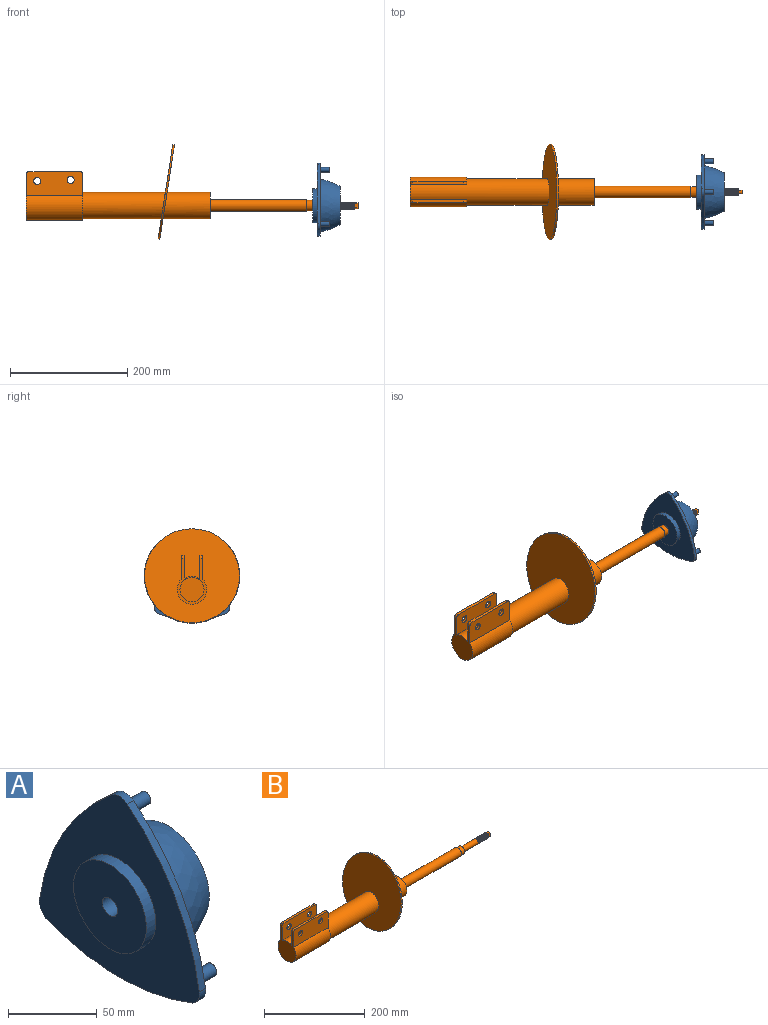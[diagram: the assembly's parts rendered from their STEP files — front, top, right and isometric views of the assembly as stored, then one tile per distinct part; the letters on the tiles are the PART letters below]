
ASSEMBLY  parts=2 mates=1
PART A: 19 faces, bbox 46.5x127.4x124.6 mm
  f0: plane 65x65mm, normal (1,0,0), area 3205.2mm2, adj f1,f6
  f1: revolved ~90x90mm, area 9080.5mm2, adj f0,f2
  f2: plane 127.41x124.63mm, normal (1,0,0), area 4430.2mm2, adj f1,f7,f8,f9,f10,f11,f12,f13
  f3: plane 127.41x124.63mm, normal (-1,0,0), area 8300.7mm2, adj f4,f7,f8,f9,f10,f11,f12
  f4: cylinder r=29mm len=58mm, axis (-1,0,0), area 1366.6mm2, adj f3,f5
  f5: plane 58x58mm, normal (-1,0,0), area 2529mm2, adj f4,f6
  f6: cylinder r=6mm len=46.5mm, axis (-1,0,0), area 1753mm2, adj f0,f5
  f7: cylinder r=158.67mm len=100.72mm, axis (1,0,0), area 593.2mm2, adj f2,f3,f11,f12
  f8: cylinder r=155.68mm len=114.78mm, axis (1,0,0), area 587.8mm2, adj f2,f3,f10,f11
  f9: cylinder r=158.65mm len=100.72mm, axis (1,0,0), area 593.2mm2, adj f2,f3,f10,f12
  f10: cylinder r=10mm len=10.73mm, axis (1,0,0), area 66.8mm2, adj f2,f3,f8,f9
  f11: cylinder r=10mm len=10.73mm, axis (1,0,0), area 66.8mm2, adj f2,f3,f7,f8
  f12: cylinder r=10mm len=12.57mm, axis (1,0,0), area 68mm2, adj f2,f3,f7,f9
  f13: cylinder r=4mm len=16mm, axis (-1,0,0), area 402.1mm2, adj f2,f14
  f14: plane 8x8mm, normal (1,0,0), area 50.3mm2, adj f13
  f15: cylinder r=4mm len=16mm, axis (-1,0,0), area 402.1mm2, adj f2,f16
  f16: plane 8x8mm, normal (1,0,0), area 50.3mm2, adj f15
  f17: cylinder r=4mm len=16mm, axis (-1,0,0), area 402.1mm2, adj f2,f18
  f18: plane 8x8mm, normal (1,0,0), area 50.3mm2, adj f17
PART B: 49 faces, bbox 569.9x167.2x165.3 mm
  f0: cylinder r=22.5mm len=80.19mm, axis (-1,0,0), area 10839.2mm2, adj f8,f10
  f1: cylinder r=6mm len=7.44mm, axis (-1,0,0), area 1.4mm2, adj f2,f33,f34
  f2: plane 7.74x5.45mm, normal (-1,0,0), area 1mm2, adj f1,f3,f33,f34
  f3: cylinder r=5.9mm len=42mm, axis (-1,0,0), area 1545.1mm2, adj f2,f4,f33,f34
  f4: plane 18x18mm, normal (1,0,0), area 145.1mm2, adj f3,f5
  f5: cylinder r=9mm len=18mm, axis (-1,0,0), area 565.5mm2, adj f4,f6
  f6: plane 20x20mm, normal (1,0,0), area 59.7mm2, adj f5,f7
  f7: cylinder r=10mm len=165mm, axis (-1,0,0), area 10367.3mm2, adj f6,f8
  f8: plane 45x45mm, normal (1,0,0), area 1276.3mm2, adj f0,f7
  f9: plane 166.3x164.36mm, normal (-0.99,0,0.15), area 18987.3mm2, adj f11,f21
  f10: plane 164.35x162.39mm, normal (0.99,0,-0.15), area 19223.6mm2, adj f0,f11
  f11: cone r=81.43mm half-angle=8.9deg, axis (0.99,0,-0.15), area 1530.6mm2, adj f9,f10
  f12: plane 86.5x5mm, normal (0,0,1), area 432.5mm2, adj f13,f19,f26,f27
  f13: plane 96.5x40.82mm, normal (0,1,0), area 3701.8mm2, adj f12,f14,f18,f20,f22,f23,f26,f27
  f14: cylinder r=25.25mm len=96.5mm, axis (-1,0,0), area 11302.8mm2, adj f13,f15,f18,f20
  f15: plane 96.5x40.82mm, normal (0,-1,0), area 3701.8mm2, adj f14,f16,f18,f20,f24,f25,f28,f29
  f16: plane 86.5x5mm, normal (0,0,1), area 432.5mm2, adj f15,f17,f28,f29
  f17: plane 96.5x40mm, normal (0,1,0), area 3623.1mm2, adj f16,f18,f20,f21,f24,f25,f28,f29
  f18: plane 78.25x50.5mm, normal (-1,0,0), area 2259.6mm2, adj f13,f14,f15,f17,f19,f21,f27,f29
  f19: plane 96.5x40mm, normal (0,-1,0), area 3623.1mm2, adj f12,f18,f20,f21,f22,f23,f26,f27
  f20: plane 78.25x50.5mm, normal (1,0,0), area 669.2mm2, adj f13,f14,f15,f17,f19,f21,f26,f28
  f21: cylinder r=22.5mm len=236.64mm, axis (-1,0,0), area 22159mm2, adj f9,f17,f18,f19,f20
  f22: cylinder r=6mm len=12mm, axis (0,-1,0), area 188.5mm2, adj f13,f19
  f23: cylinder r=6mm len=12mm, axis (0,-1,0), area 188.5mm2, adj f13,f19
  f24: cylinder r=6mm len=12mm, axis (0,-1,0), area 188.5mm2, adj f15,f17
  f25: cylinder r=6mm len=12mm, axis (0,-1,0), area 188.5mm2, adj f15,f17
  f26: cylinder r=5mm len=5mm, axis (0,1,0), area 39.3mm2, adj f12,f13,f19,f20
  f27: cylinder r=5mm len=5mm, axis (0,1,0), area 39.3mm2, adj f12,f13,f18,f19
  f28: cylinder r=5mm len=5mm, axis (0,1,0), area 39.3mm2, adj f15,f16,f17,f20
  f29: cylinder r=5mm len=5mm, axis (0,1,0), area 39.3mm2, adj f15,f16,f17,f18
  f30: bspline ~29.79x13.56mm, area 968.4mm2, adj f31,f32,f33,f35,f41
  f31: plane 1.21x0.88mm, normal (0,0,1), area 0.7mm2, adj f30,f32,f35,f41,f42
  f32: bspline ~13.86x12mm, area 3.7mm2, adj f30,f31,f41,f42
  f33: plane 1.27x1.16mm, normal (0,-0.95,-0.31), area 0.7mm2, adj f1,f2,f3,f30,f34,f35
  f34: bspline ~13.55x13.18mm, area 2.4mm2, adj f1,f2,f3,f33,f35
  f35: bspline ~29.62x11.71mm, area 969mm2, adj f30,f31,f33,f34
  f36: plane 10x6mm, normal (1,0,0), area 56.2mm2, adj f37,f38,f39,f40
  f37: plane 8x6mm, normal (0,-1,0), area 48mm2, adj f36,f38,f40,f41
  f38: cylinder r=5mm len=6mm, axis (-1,0,0), area 38.6mm2, adj f36,f37,f39,f41
  f39: plane 8x6mm, normal (0,1,0), area 48mm2, adj f36,f38,f40,f41
  f40: cylinder r=5mm len=6mm, axis (-1,0,0), area 38.6mm2, adj f36,f37,f39,f41
  f41: plane 12.37x12.15mm, normal (1,0,0), area 51.9mm2, adj f30,f31,f32,f37,f38,f39,f40,f42
  f42: cylinder r=6mm len=12mm, axis (-1,0,0), area 9.6mm2, adj f31,f32,f41
  f43: plane 41x41mm, normal (-1,0,0), area 1320.3mm2, adj f44
  f44: cylinder r=20.5mm len=77.88mm, axis (-1,0,0), area 9618.1mm2, adj f43,f45
  f45: plane 42.35x42.35mm, normal (0.99,0,-0.15), area 1336.3mm2, adj f44
  f46: cylinder r=20.5mm len=235.03mm, axis (-1,0,0), area 29860.7mm2, adj f47,f48
  f47: plane 41x41mm, normal (1,0,0), area 1320.3mm2, adj f46
  f48: plane 42.35x42.35mm, normal (-0.99,0,0.15), area 1336.3mm2, adj f46
PLACE A t=(-15.13,-5.39,-29.95)mm
PLACE B t=(-503.63,-5.39,-29.95)mm
MATE fastened B.f0 <-> A.f4  axis (-1,0,0) through (-15.13,-5.39,-29.95)mm
